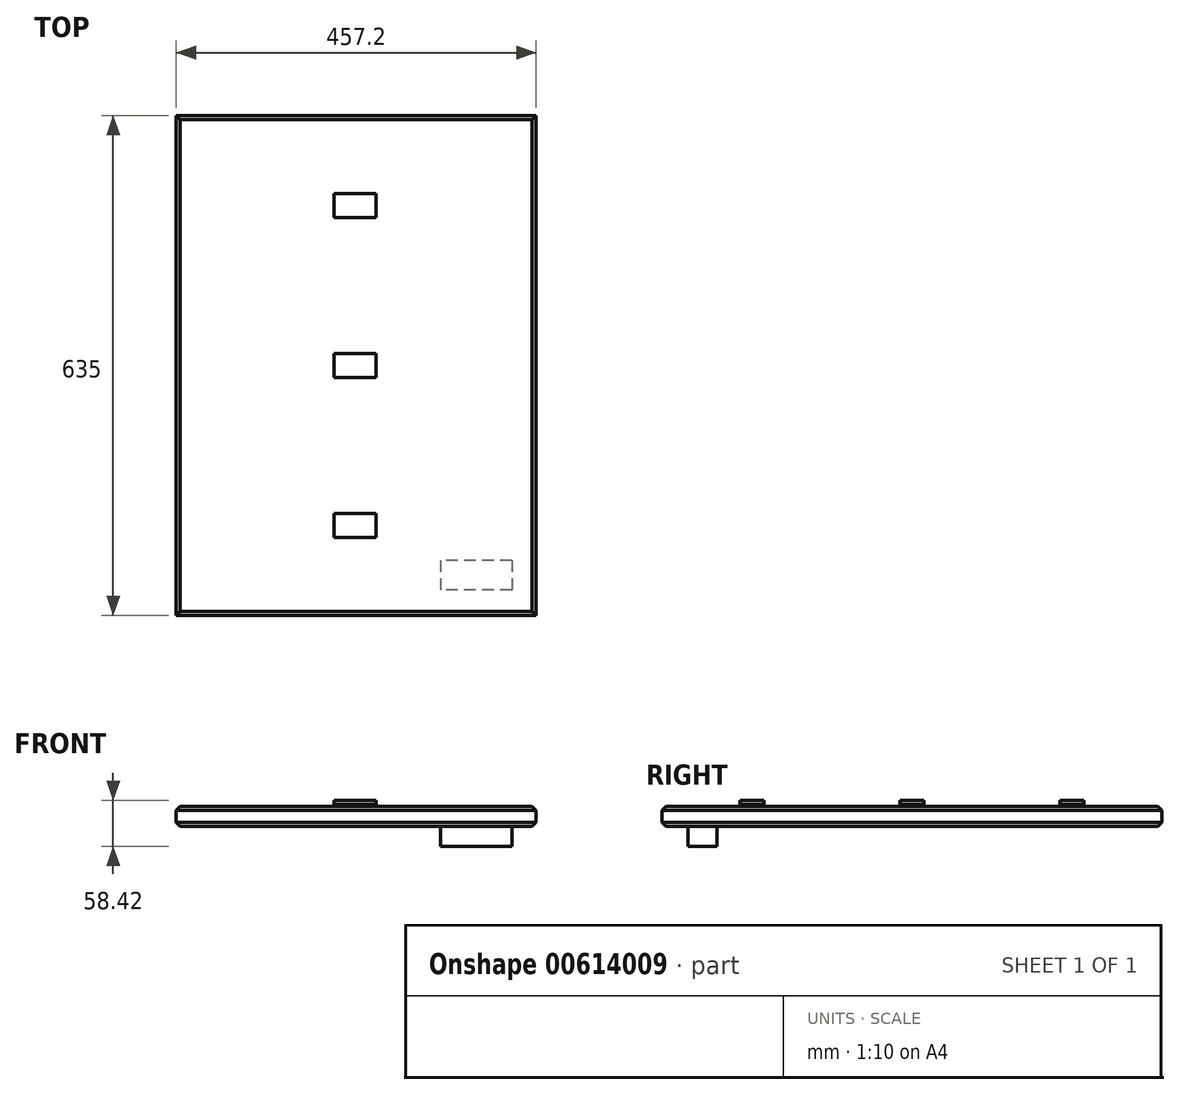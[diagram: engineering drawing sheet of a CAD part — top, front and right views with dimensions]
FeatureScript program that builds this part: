
annotation { "Feature Type Name" : "Feature", "Feature Type Description" : "" }
export const myFeature = defineFeature(function(context is Context, id is Id, definition is map)
    precondition{}
    {
        {
            var Q0;
            Q0=qCreatedBy(makeId("Top.planeOp"),FACE);
            var sketch = newSketch(context, id + "F0", { "sketchPlane" : qUnion([Q0])});
            skLineSegment(sketch, "E0.bottom", {"start": v(-228.6, 317.5) * mm, "end": v(228.6, 317.5) * mm});
            skLineSegment(sketch, "E0.top", {"start": v(-228.6, -317.5) * mm, "end": v(228.6, -317.5) * mm});
            skLineSegment(sketch, "E0.left", {"start": v(-228.6, 317.5) * mm, "end": v(-228.6, -317.5) * mm});
            skLineSegment(sketch, "E0.right", {"start": v(228.6, 317.5) * mm, "end": v(228.6, -317.5) * mm});
            skPoint(sketch, "E0.middle", {"position": v(0, 0) * mm});
            skSolve(sketch);
        }
        {
            var Q0;
            Q0 = qSketchRegion(id + "F0", true);
            extrude(context, id + "F1", {"entities" : qUnion([Q0]), "depth" : 25.4 * mm, "offsetDistance" : 25.4 * mm});
        }
        {
            var Q0;
            Q0=makeQuery(id+"F1.opExtrude","CAP_EDGE",EDGE,{"disambiguationData":[OSD([sQuery(id+"F0.wireOp",EDGE,"E0.top")])],"isStart":false});
            var Q1;
            Q1=makeQuery(id+"F1.opExtrude","CAP_EDGE",EDGE,{"disambiguationData":[OSD([sQuery(id+"F0.wireOp",EDGE,"E0.left")])],"isStart":false});
            var Q2;
            Q2=makeQuery(id+"F1.opExtrude","CAP_EDGE",EDGE,{"disambiguationData":[OSD([sQuery(id+"F0.wireOp",EDGE,"E0.bottom")])],"isStart":false});
            var Q3;
            Q3=makeQuery(id+"F1.opExtrude","CAP_EDGE",EDGE,{"disambiguationData":[OSD([sQuery(id+"F0.wireOp",EDGE,"E0.right")])],"isStart":false});
            var Q4;
            Q4=makeQuery(id+"F1.opExtrude","CAP_EDGE",EDGE,{"disambiguationData":[OSD([sQuery(id+"F0.wireOp",EDGE,"E0.right")])],"isStart":true});
            var Q5;
            Q5=makeQuery(id+"F1.opExtrude","CAP_EDGE",EDGE,{"disambiguationData":[OSD([sQuery(id+"F0.wireOp",EDGE,"E0.top")])],"isStart":true});
            var Q6;
            Q6=makeQuery(id+"F1.opExtrude","CAP_EDGE",EDGE,{"disambiguationData":[OSD([sQuery(id+"F0.wireOp",EDGE,"E0.left")])],"isStart":true});
            var Q7;
            Q7=makeQuery(id+"F1.opExtrude","CAP_EDGE",EDGE,{"disambiguationData":[OSD([sQuery(id+"F0.wireOp",EDGE,"E0.bottom")])],"isStart":true});
            chamfer(context, id + "F2", {"entities" : qUnion([Q0, Q1, Q2, Q3, Q4, Q5, Q6, Q7]), "width" : 5.08 * mm, "tangentPropagation" : true});
        }
        {
            var Q0;
            Q0=makeQuery(id+"F1.opExtrude","CAP_FACE",FACE,{"disambiguationData":[OSD([sQuery(id+"F0.wireOp",EDGE,"E0.bottom"),sQuery(id+"F0.wireOp",EDGE,"E0.top"),sQuery(id+"F0.wireOp",EDGE,"E0.left"),sQuery(id+"F0.wireOp",EDGE,"E0.right")])],"isStart":true});
            var sketch = newSketch(context, id + "F3", { "sketchPlane" : qUnion([Q0])});
            skLineSegment(sketch, "E1.bottom", {"start": v(197.87, 247.58) * mm, "end": v(107.2, 247.58) * mm});
            skLineSegment(sketch, "E1.top", {"start": v(197.87, 284.92) * mm, "end": v(107.2, 284.92) * mm});
            skLineSegment(sketch, "E1.left", {"start": v(197.87, 247.58) * mm, "end": v(197.87, 284.92) * mm});
            skLineSegment(sketch, "E1.right", {"start": v(107.2, 247.58) * mm, "end": v(107.2, 284.92) * mm});
            skSolve(sketch);
        }
        {
            var Q0;
            Q0=makeQuery(id+"F3.imprint","IMPRINT",FACE,{"disambiguationData":[TD([[makeQuery(id+"F3.imprint","IMPRINT",EDGE,{"derivedFrom":sQuery(id+"F3.wireOp",EDGE,"E1.bottom")}),-1.0]])]});
            extrude(context, id + "F4", {"entities" : qUnion([Q0]), "operationType" : NewBodyOperationType.ADD, "depth" : 25.4 * mm, "offsetDistance" : 25.4 * mm});
        }
        {
            var Q0;
            Q0=qCreatedBy(makeId("Top.planeOp"),FACE);
            var sketch = newSketch(context, id + "F5", { "sketchPlane" : qUnion([Q0])});
            skLineSegment(sketch, "E2.bottom", {"start": v(-698.37, 114.43) * mm, "end": v(-751.7, 114.43) * mm});
            skLineSegment(sketch, "E2.top", {"start": v(-698.37, 144.91) * mm, "end": v(-751.7, 144.91) * mm});
            skLineSegment(sketch, "E2.left", {"start": v(-698.37, 114.43) * mm, "end": v(-698.37, 144.91) * mm});
            skLineSegment(sketch, "E2.right", {"start": v(-751.7, 114.43) * mm, "end": v(-751.7, 144.91) * mm});
            skPoint(sketch, "E2.middle", {"position": v(-725.04, 129.67) * mm});
            skSolve(sketch);
        }
        {
            var Q0;
            Q0 = qSketchRegion(id + "F5", true);
            extrude(context, id + "F6", {"entities" : qUnion([Q0]), "depth" : 5.08 * mm, "offsetDistance" : 25.4 * mm});
        }
        {
            var Q0;
            Q0=makeQuery(id+"F6.opExtrude","SWEPT_BODY",BODY,{"disambiguationData":[OSD([sQuery(id+"F5.wireOp",EDGE,"E2.bottom"),sQuery(id+"F5.wireOp",EDGE,"E2.top"),sQuery(id+"F5.wireOp",EDGE,"E2.left"),sQuery(id+"F5.wireOp",EDGE,"E2.right")])]});
            transform(context, id + "F7", {"entities" : qUnion([Q0]), "transformType" : TransformType.TRANSLATION_3D, "dx" : 0 * mm, "dy" : 203.2 * mm, "dz" : 0 * mm, "makeCopy" : true});
        }
        {
            var Q0;
            Q0=makeQuery(id+"F6.opExtrude","SWEPT_BODY",BODY,{"disambiguationData":[OSD([sQuery(id+"F5.wireOp",EDGE,"E2.bottom"),sQuery(id+"F5.wireOp",EDGE,"E2.top"),sQuery(id+"F5.wireOp",EDGE,"E2.left"),sQuery(id+"F5.wireOp",EDGE,"E2.right")])]});
            transform(context, id + "F8", {"entities" : qUnion([Q0]), "transformType" : TransformType.TRANSLATION_3D, "dx" : 0 * mm, "dy" : -203.2 * mm, "dz" : 0 * mm, "makeCopy" : true});
        }
        {
            var Q0;
            Q0=makeQuery(id+"F8.opPattern","COPY",BODY,{"derivedFrom":makeQuery(id+"F6.opExtrude","SWEPT_BODY",BODY,{"disambiguationData":[OSD([sQuery(id+"F5.wireOp",EDGE,"E2.bottom"),sQuery(id+"F5.wireOp",EDGE,"E2.top"),sQuery(id+"F5.wireOp",EDGE,"E2.left"),sQuery(id+"F5.wireOp",EDGE,"E2.right")])]}),"instanceName":"1"});
            var Q1;
            Q1=makeQuery(id+"F7.opPattern","COPY",BODY,{"derivedFrom":makeQuery(id+"F6.opExtrude","SWEPT_BODY",BODY,{"disambiguationData":[OSD([sQuery(id+"F5.wireOp",EDGE,"E2.bottom"),sQuery(id+"F5.wireOp",EDGE,"E2.top"),sQuery(id+"F5.wireOp",EDGE,"E2.left"),sQuery(id+"F5.wireOp",EDGE,"E2.right")])]}),"instanceName":"1"});
            var Q2;
            Q2=makeQuery(id+"F6.opExtrude","SWEPT_BODY",BODY,{"disambiguationData":[OSD([sQuery(id+"F5.wireOp",EDGE,"E2.bottom"),sQuery(id+"F5.wireOp",EDGE,"E2.top"),sQuery(id+"F5.wireOp",EDGE,"E2.left"),sQuery(id+"F5.wireOp",EDGE,"E2.right")])]});
            transform(context, id + "F9", {"entities" : qUnion([Q0, Q1, Q2]), "transformType" : TransformType.TRANSLATION_3D, "dx" : 723.9 * mm, "dy" : -129.54 * mm, "dz" : 27.94 * mm, "makeCopy" : false});
        }
    });
